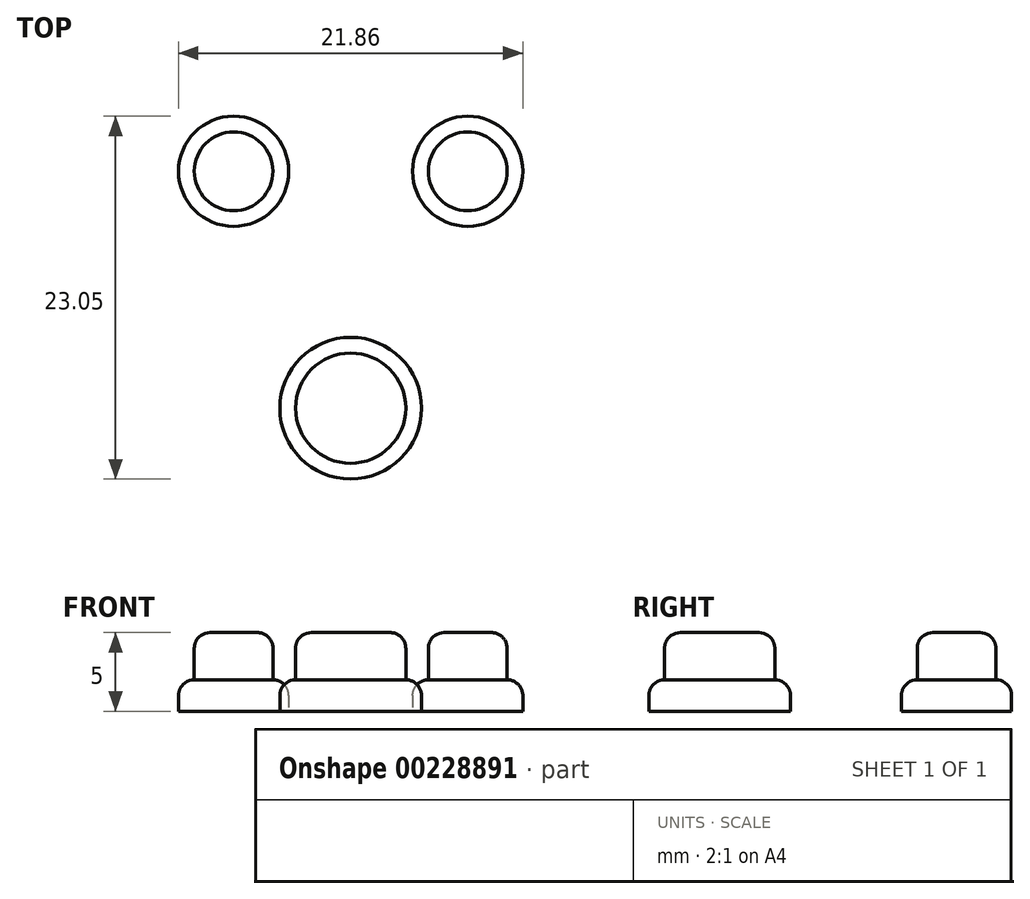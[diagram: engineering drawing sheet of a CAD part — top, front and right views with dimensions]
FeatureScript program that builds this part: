
annotation { "Feature Type Name" : "Feature", "Feature Type Description" : "" }
export const myFeature = defineFeature(function(context is Context, id is Id, definition is map)
    precondition{}
    {
        {
            var Q0;
            Q0=qCreatedBy(makeId("Top.planeOp"),FACE);
            var sketch = newSketch(context, id + "F0", { "sketchPlane" : qUnion([Q0])});
            skPoint(sketch, "E0", {"position": v(-7.43, 7.15) * mm});
            skCircle(sketch, "E1", {"center": v(-7.43, 7.15) * mm, "radius": 3.5 * mm});
            skPoint(sketch, "E2", {"position": v(0, -7.9) * mm});
            skCircle(sketch, "E3", {"center": v(0, -7.9) * mm, "radius": 4.5 * mm});
            skSolve(sketch);
        }
        {
            var Q0;
            Q0 = qSketchRegion(id + "F0", true);
            extrude(context, id + "F1", {"entities" : qUnion([Q0]), "depth" : 2 * mm, "offsetDistance" : 25 * mm});
        }
        {
            var Q0;
            Q0=makeQuery(id+"F1.opExtrude","CAP_FACE",FACE,{"disambiguationData":[OSD([sQuery(id+"F0.wireOp",EDGE,"E1")])],"isStart":false});
            var sketch = newSketch(context, id + "F2", { "sketchPlane" : qUnion([Q0])});
            skCircle(sketch, "E4", {"center": v(-7.43, 7.15) * mm, "radius": 2.5 * mm});
            skCircle(sketch, "E5", {"center": v(0, -7.9) * mm, "radius": 3.5 * mm});
            skSolve(sketch);
        }
        {
            var Q0;
            Q0 = qSketchRegion(id + "F2", true);
            extrude(context, id + "F3", {"entities" : qUnion([Q0]), "depth" : 3 * mm, "offsetDistance" : 25 * mm});
        }
        {
            var Q0;
            Q0=makeQuery(id+"F1.opExtrude","SWEPT_BODY",BODY,{"disambiguationData":[OSD([sQuery(id+"F0.wireOp",EDGE,"E1")])]});
            var Q1;
            Q1=makeQuery(id+"F3.opExtrude","SWEPT_BODY",BODY,{"disambiguationData":[OSD([sQuery(id+"F2.wireOp",EDGE,"E4")])]});
            var Q2;
            Q2=qCreatedBy(makeId("Right.planeOp"),FACE);
            mirror(context, id + "F4", {"entities" : qUnion([Q0, Q1]), "mirrorPlane" : qUnion([Q2])});
        }
        {
            var Q0;
            Q0=makeQuery(id+"F3.opExtrude","CAP_EDGE",EDGE,{"disambiguationData":[OSD([sQuery(id+"F2.wireOp",EDGE,"E4")])],"isStart":false});
            var Q1;
            Q1=makeQuery(id+"F4.opPattern","COPY",EDGE,{"derivedFrom":makeQuery(id+"F3.opExtrude","CAP_EDGE",EDGE,{"disambiguationData":[OSD([sQuery(id+"F2.wireOp",EDGE,"E4")])],"isStart":false}),"instanceName":"1"});
            var Q2;
            Q2=makeQuery(id+"F3.opExtrude","CAP_EDGE",EDGE,{"disambiguationData":[OSD([sQuery(id+"F2.wireOp",EDGE,"E5")])],"isStart":false});
            var Q3;
            Q3=makeQuery(id+"F1.opExtrude","CAP_EDGE",EDGE,{"disambiguationData":[OSD([sQuery(id+"F0.wireOp",EDGE,"E1")])],"isStart":false});
            var Q4;
            Q4=makeQuery(id+"F4.opPattern","COPY",EDGE,{"derivedFrom":makeQuery(id+"F1.opExtrude","CAP_EDGE",EDGE,{"disambiguationData":[OSD([sQuery(id+"F0.wireOp",EDGE,"E1")])],"isStart":false}),"instanceName":"1"});
            var Q5;
            Q5=makeQuery(id+"F1.opExtrude","CAP_EDGE",EDGE,{"disambiguationData":[OSD([sQuery(id+"F0.wireOp",EDGE,"E3")])],"isStart":false});
            fillet(context, id + "F5", {"entities" : qUnion([Q0, Q1, Q2, Q3, Q4, Q5]), "tangentPropagation" : true, "radius" : 1 * mm, "defaultsChanged" : false, "vertexSettings" : [], "allowEdgeOverflow" : false});
        }
    });
